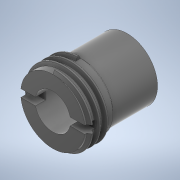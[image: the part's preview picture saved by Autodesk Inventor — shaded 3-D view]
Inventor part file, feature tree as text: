
AUTODESK INVENTOR PART (.ipt)
format: ipt  version: 2020 (Build 240168000, 168)  size: 288,768 bytes
history: native  units: mm
features: sketch x5, extrude x3, sweep x1, chamfer x1, projected_geometry x1, other x1
ambient origin geometry x8: Origin, YZ Plane, XZ Plane, XY Plane, X Axis, Y Axis, Z Axis, Center Point
bodies: Solid1 (feature_tree)
feature tree (12):
  extrude  "Extrusion1"  Depth=7.0mm
  extrude  "Extrusion2"  Depth=5.5mm
  sweep  "Sweep1"
  extrude  "Extrusion3"  Depth=2.0mm
  chamfer  "Chamfer1"  Distance=0.45mm
  sketch  "Sketch1"  dims[d0=12.7mm d1=7.0mm]
  sketch  "Sketch2"  dims[d2=5.5mm d3=0.0mm d4=12.0mm]
  sketch  "Sketch3"  dims[d5=9.2mm d6=0.0mm d10=1.5mm d11=30.0mm d12=12.7mm d13=0.0mm]
  projected_geometry  "Projected Loop1"
  sketch  "3D Sketch1"
  other  "Helical Curve1"
  sketch  "Sketch4"  dims[d14=1.0mm d15=0.2mm d16=0.45mm d17=0.0mm d18=0.0mm d19=20.0mm d20=1.5mm d21=2.0mm d22=0.0mm d23=0.35mm d24=2.0mm d25=45.0deg]
